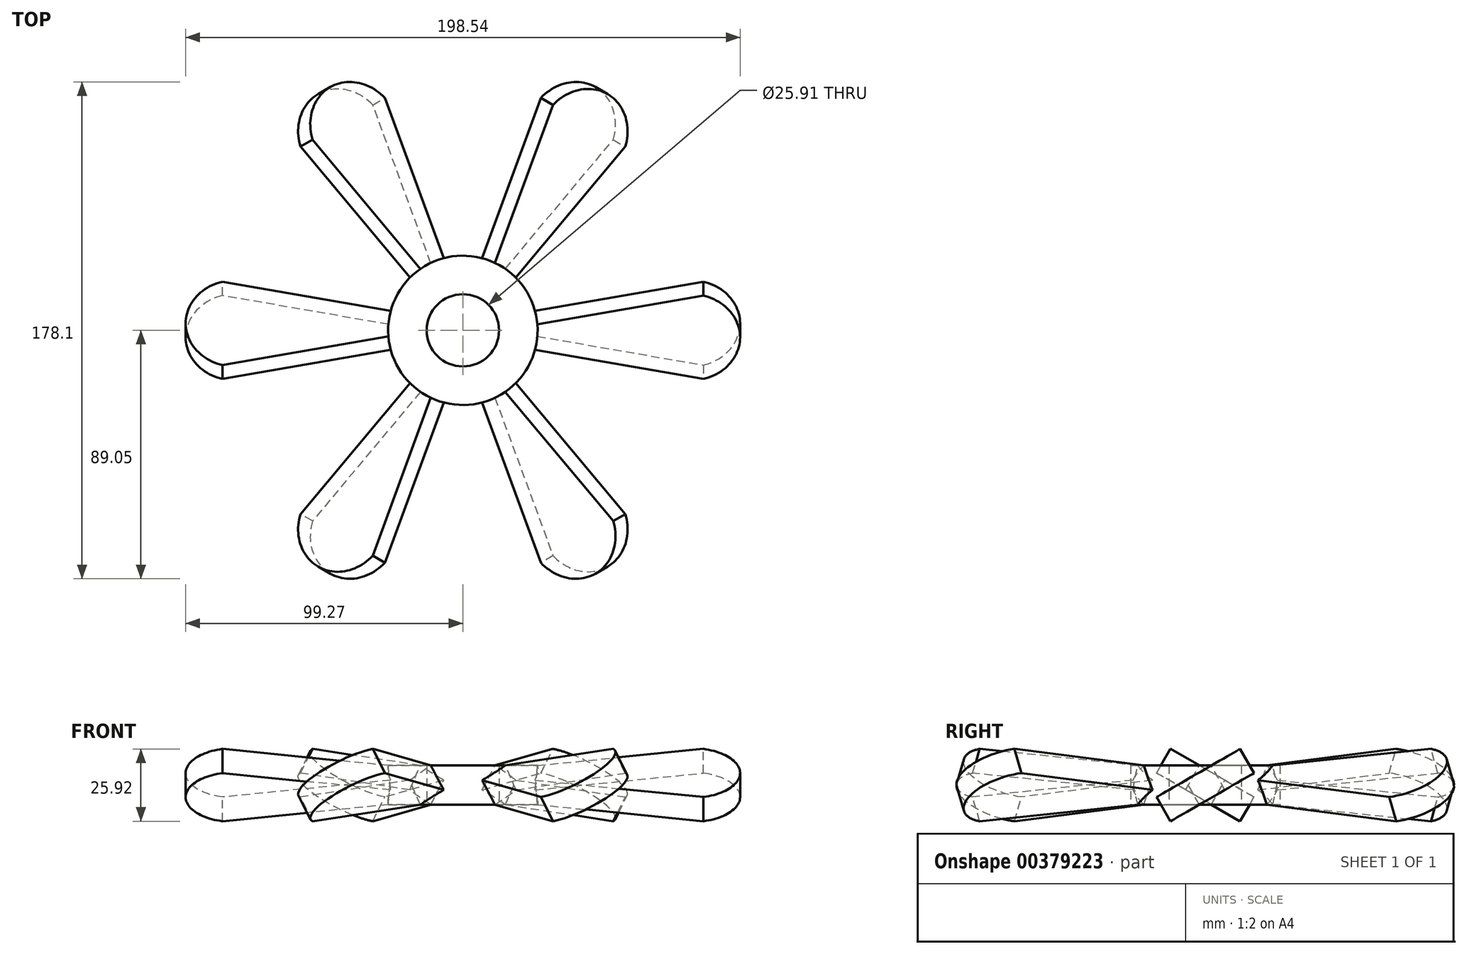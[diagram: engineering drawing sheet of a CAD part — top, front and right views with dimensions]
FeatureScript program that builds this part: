
annotation { "Feature Type Name" : "Feature", "Feature Type Description" : "" }
export const myFeature = defineFeature(function(context is Context, id is Id, definition is map)
    precondition{}
    {
        {
            var Q0;
            Q0=qCreatedBy(makeId("Top.planeOp"),FACE);
            var sketch = newSketch(context, id + "F0", { "sketchPlane" : qUnion([Q0])});
            skLineSegment(sketch, "E0", {"start": v(0, 0) * mm, "end": v(86.12, 17.27) * mm});
            skLineSegment(sketch, "E1", {"start": v(3.06, 0) * mm, "end": v(66.89, 0) * mm, "construction": true});
            skLineSegment(sketch, "E2.MirrorCS", {"start": v(0, 0) * mm, "end": v(86.12, -17.27) * mm});
            skArc(sketch, "E3", {"start": v(86.12, -17.27) * mm, "mid": v(99.27, 0) * mm, "end": v(86.12, 17.27) * mm});
            skSolve(sketch);
        }
        {
            var Q0;
            Q0=makeQuery(id+"F0.imprint","IMPRINT",FACE,{"disambiguationData":[TD([[makeQuery(id+"F0.imprint","IMPRINT",EDGE,{"derivedFrom":sQuery(id+"F0.wireOp",EDGE,"E0")}),-1.0]])]});
            extrude(context, id + "F1", {"entities" : qUnion([Q0]), "endBound" : BoundingType.SYMMETRIC, "oppositeDirection" : true, "depth" : 10 * mm});
        }
        {
            var Q0;
            Q0=qCreatedBy(makeId("Top.planeOp"),FACE);
            var sketch = newSketch(context, id + "F2", { "sketchPlane" : qUnion([Q0])});
            skLineSegment(sketch, "E4", {"start": v(0, 0) * mm, "end": v(111.92, 0) * mm});
            skSolve(sketch);
        }
        {
            var Q0;
            Q0=makeQuery(id+"F1.opExtrude","SWEPT_BODY",BODY,{"disambiguationData":[OSD([sQuery(id+"F0.wireOp",EDGE,"E0"),sQuery(id+"F0.wireOp",EDGE,"E2.MirrorCS"),sQuery(id+"F0.wireOp",EDGE,"E3")])]});
            var Q1;
            Q1=sQuery(id+"F2.wireOp",EDGE,"E4");
            transform(context, id + "F3", {"entities" : qUnion([Q0]), "transformType" : TransformType.ROTATION, "transformAxis" : qUnion([Q1]), "angle" : 30 * degree, "makeCopy" : false});
        }
        {
            var Q0;
            Q0=qCreatedBy(makeId("Front.planeOp"),FACE);
            var sketch = newSketch(context, id + "F4", { "sketchPlane" : qUnion([Q0])});
            skLineSegment(sketch, "E5", {"start": v(0, 0) * mm, "end": v(0, 41.33) * mm, "construction": true});
            skSolve(sketch);
        }
        {
            var Q0;
            Q0=makeQuery(id+"F1.opExtrude","SWEPT_BODY",BODY,{"disambiguationData":[OSD([sQuery(id+"F0.wireOp",EDGE,"E0"),sQuery(id+"F0.wireOp",EDGE,"E2.MirrorCS"),sQuery(id+"F0.wireOp",EDGE,"E3")])]});
            var Q1;
            Q1=sQuery(id+"F4.wireOp",EDGE,"E5");
            circularPattern(context, id + "F5", {"entities" : qUnion([Q0]), "axis" : qUnion([Q1]), "angle" : 360 * degree, "instanceCount" : 6, "equalSpace" : true});
        }
        {
            var Q0;
            Q0=qCreatedBy(makeId("Top.planeOp"),FACE);
            var sketch = newSketch(context, id + "F6", { "sketchPlane" : qUnion([Q0])});
            skCircle(sketch, "E6", {"center": v(0, 0) * mm, "radius": 26.76 * mm});
            skSolve(sketch);
        }
        {
            var Q0;
            Q0=makeQuery(id+"F6.imprint","IMPRINT",FACE,{"disambiguationData":[TD([[makeQuery(id+"F6.imprint","IMPRINT",EDGE,{"derivedFrom":sQuery(id+"F6.wireOp",EDGE,"E6")}),1.0]])]});
            extrude(context, id + "F7", {"entities" : qUnion([Q0]), "endBound" : BoundingType.SYMMETRIC, "depth" : 20 * mm});
        }
        {
            var Q0;
            Q0=makeQuery(id+"F1.opExtrude","SWEPT_BODY",BODY,{"disambiguationData":[OSD([sQuery(id+"F0.wireOp",EDGE,"E0"),sQuery(id+"F0.wireOp",EDGE,"E2.MirrorCS"),sQuery(id+"F0.wireOp",EDGE,"E3")])]});
            var Q1;
            Q1=makeQuery(id+"F5.opPattern","COPY",BODY,{"derivedFrom":makeQuery(id+"F1.opExtrude","SWEPT_BODY",BODY,{"disambiguationData":[OSD([sQuery(id+"F0.wireOp",EDGE,"E0"),sQuery(id+"F0.wireOp",EDGE,"E2.MirrorCS"),sQuery(id+"F0.wireOp",EDGE,"E3")])]}),"instanceName":"1"});
            var Q2;
            Q2=makeQuery(id+"F5.opPattern","COPY",BODY,{"derivedFrom":makeQuery(id+"F1.opExtrude","SWEPT_BODY",BODY,{"disambiguationData":[OSD([sQuery(id+"F0.wireOp",EDGE,"E0"),sQuery(id+"F0.wireOp",EDGE,"E2.MirrorCS"),sQuery(id+"F0.wireOp",EDGE,"E3")])]}),"instanceName":"2"});
            var Q3;
            Q3=makeQuery(id+"F5.opPattern","COPY",BODY,{"derivedFrom":makeQuery(id+"F1.opExtrude","SWEPT_BODY",BODY,{"disambiguationData":[OSD([sQuery(id+"F0.wireOp",EDGE,"E0"),sQuery(id+"F0.wireOp",EDGE,"E2.MirrorCS"),sQuery(id+"F0.wireOp",EDGE,"E3")])]}),"instanceName":"3"});
            var Q4;
            Q4=makeQuery(id+"F5.opPattern","COPY",BODY,{"derivedFrom":makeQuery(id+"F1.opExtrude","SWEPT_BODY",BODY,{"disambiguationData":[OSD([sQuery(id+"F0.wireOp",EDGE,"E0"),sQuery(id+"F0.wireOp",EDGE,"E2.MirrorCS"),sQuery(id+"F0.wireOp",EDGE,"E3")])]}),"instanceName":"4"});
            var Q5;
            Q5=makeQuery(id+"F5.opPattern","COPY",BODY,{"derivedFrom":makeQuery(id+"F1.opExtrude","SWEPT_BODY",BODY,{"disambiguationData":[OSD([sQuery(id+"F0.wireOp",EDGE,"E0"),sQuery(id+"F0.wireOp",EDGE,"E2.MirrorCS"),sQuery(id+"F0.wireOp",EDGE,"E3")])]}),"instanceName":"5"});
            var Q6;
            Q6=makeQuery(id+"F7.opExtrude","SWEPT_BODY",BODY,{"disambiguationData":[OSD([sQuery(id+"F6.wireOp",EDGE,"E6")])]});
            booleanBodies(context, id + "F8", {"operationType" : BooleanOperationType.UNION, "tools" : qUnion([Q0, Q1, Q2, Q3, Q4, Q5, Q6])});
        }
        {
            var Q0;
            {var subQ0=sQuery(id+"F0.wireOp",EDGE,"E0");Q0=makeQuery(id+"F8.opBoolean","INTERSECT",VERTEX,{"derivedFrom":[makeQuery(id+"F5.opPattern","COPY",FACE,{"derivedFrom":makeQuery(id+"F1.opExtrude","SWEPT_FACE",FACE,{"disambiguationData":[OSD([subQ0])]}),"instanceName":"3"}),makeQuery(id+"F5.opPattern","COPY",FACE,{"derivedFrom":makeQuery(id+"F1.opExtrude","CAP_FACE",FACE,{"disambiguationData":[OSD([subQ0,sQuery(id+"F0.wireOp",EDGE,"E2.MirrorCS"),sQuery(id+"F0.wireOp",EDGE,"E3")])],"isStart":true}),"instanceName":"3"}),makeQuery(id+"F7.opExtrude","SWEPT_FACE",FACE,{"disambiguationData":[OSD([sQuery(id+"F6.wireOp",EDGE,"E6")])]})]});}
            var Q1;
            {var subQ0=sQuery(id+"F0.wireOp",EDGE,"E0");Q1=makeQuery(id+"F8.opBoolean","INTERSECT",VERTEX,{"derivedFrom":[makeQuery(id+"F5.opPattern","COPY",FACE,{"derivedFrom":makeQuery(id+"F1.opExtrude","SWEPT_FACE",FACE,{"disambiguationData":[OSD([subQ0])]}),"instanceName":"4"}),makeQuery(id+"F5.opPattern","COPY",FACE,{"derivedFrom":makeQuery(id+"F1.opExtrude","CAP_FACE",FACE,{"disambiguationData":[OSD([subQ0,sQuery(id+"F0.wireOp",EDGE,"E2.MirrorCS"),sQuery(id+"F0.wireOp",EDGE,"E3")])],"isStart":true}),"instanceName":"4"}),makeQuery(id+"F7.opExtrude","SWEPT_FACE",FACE,{"disambiguationData":[OSD([sQuery(id+"F6.wireOp",EDGE,"E6")])]})]});}
            var Q2;
            {var subQ0=sQuery(id+"F0.wireOp",EDGE,"E0");Q2=makeQuery(id+"F8.opBoolean","INTERSECT",VERTEX,{"derivedFrom":[makeQuery(id+"F1.opExtrude","SWEPT_FACE",FACE,{"disambiguationData":[OSD([subQ0])]}),makeQuery(id+"F1.opExtrude","CAP_FACE",FACE,{"disambiguationData":[OSD([subQ0,sQuery(id+"F0.wireOp",EDGE,"E2.MirrorCS"),sQuery(id+"F0.wireOp",EDGE,"E3")])],"isStart":true}),makeQuery(id+"F7.opExtrude","SWEPT_FACE",FACE,{"disambiguationData":[OSD([sQuery(id+"F6.wireOp",EDGE,"E6")])]})]});}
            cPlane(context, id + "F9", {"entities" : qUnion([Q0, Q1, Q2]), "cplaneType" : CPlaneType.THREE_POINT, "offset" : 25 * mm, "width" : 150 * mm, "height" : 150 * mm});
        }
        {
            var Q0;
            Q0=makeQuery(id+"F7.opExtrude","CAP_FACE",FACE,{"disambiguationData":[OSD([sQuery(id+"F6.wireOp",EDGE,"E6")])],"isStart":false});
            var Q1;
            Q1=qCreatedBy(id+"F9.planeOp",FACE);
            extrude(context, id + "F10", {"entities" : qUnion([Q0]), "operationType" : NewBodyOperationType.REMOVE, "endBound" : BoundingType.UP_TO_SURFACE, "oppositeDirection" : true, "endBoundEntityFace" : qUnion([Q1]), "depth" : 25 * mm});
        }
        {
            var Q0;
            {var subQ0=sQuery(id+"F0.wireOp",EDGE,"E2.MirrorCS");Q0=makeQuery(id+"F8.opBoolean","INTERSECT",VERTEX,{"derivedFrom":[makeQuery(id+"F5.opPattern","COPY",FACE,{"derivedFrom":makeQuery(id+"F1.opExtrude","CAP_FACE",FACE,{"disambiguationData":[OSD([sQuery(id+"F0.wireOp",EDGE,"E0"),subQ0,sQuery(id+"F0.wireOp",EDGE,"E3")])],"isStart":false}),"instanceName":"2"}),makeQuery(id+"F5.opPattern","COPY",FACE,{"derivedFrom":makeQuery(id+"F1.opExtrude","SWEPT_FACE",FACE,{"disambiguationData":[OSD([subQ0])]}),"instanceName":"2"}),makeQuery(id+"F7.opExtrude","SWEPT_FACE",FACE,{"disambiguationData":[OSD([sQuery(id+"F6.wireOp",EDGE,"E6")])]})]});}
            var Q1;
            {var subQ0=sQuery(id+"F0.wireOp",EDGE,"E2.MirrorCS");Q1=makeQuery(id+"F8.opBoolean","INTERSECT",VERTEX,{"derivedFrom":[makeQuery(id+"F5.opPattern","COPY",FACE,{"derivedFrom":makeQuery(id+"F1.opExtrude","CAP_FACE",FACE,{"disambiguationData":[OSD([sQuery(id+"F0.wireOp",EDGE,"E0"),subQ0,sQuery(id+"F0.wireOp",EDGE,"E3")])],"isStart":false}),"instanceName":"1"}),makeQuery(id+"F5.opPattern","COPY",FACE,{"derivedFrom":makeQuery(id+"F1.opExtrude","SWEPT_FACE",FACE,{"disambiguationData":[OSD([subQ0])]}),"instanceName":"1"}),makeQuery(id+"F7.opExtrude","SWEPT_FACE",FACE,{"disambiguationData":[OSD([sQuery(id+"F6.wireOp",EDGE,"E6")])]})]});}
            var Q2;
            {var subQ0=sQuery(id+"F0.wireOp",EDGE,"E2.MirrorCS");Q2=makeQuery(id+"F8.opBoolean","INTERSECT",VERTEX,{"derivedFrom":[makeQuery(id+"F5.opPattern","COPY",FACE,{"derivedFrom":makeQuery(id+"F1.opExtrude","CAP_FACE",FACE,{"disambiguationData":[OSD([sQuery(id+"F0.wireOp",EDGE,"E0"),subQ0,sQuery(id+"F0.wireOp",EDGE,"E3")])],"isStart":false}),"instanceName":"5"}),makeQuery(id+"F5.opPattern","COPY",FACE,{"derivedFrom":makeQuery(id+"F1.opExtrude","SWEPT_FACE",FACE,{"disambiguationData":[OSD([subQ0])]}),"instanceName":"5"}),makeQuery(id+"F7.opExtrude","SWEPT_FACE",FACE,{"disambiguationData":[OSD([sQuery(id+"F6.wireOp",EDGE,"E6")])]})]});}
            cPlane(context, id + "F11", {"entities" : qUnion([Q0, Q1, Q2]), "cplaneType" : CPlaneType.THREE_POINT, "offset" : 25 * mm, "width" : 150 * mm, "height" : 150 * mm});
        }
        {
            var Q0;
            Q0=makeQuery(id+"F7.opExtrude","CAP_FACE",FACE,{"disambiguationData":[OSD([sQuery(id+"F6.wireOp",EDGE,"E6")])],"isStart":true});
            var Q1;
            Q1=qCreatedBy(id+"F11.planeOp",FACE);
            extrude(context, id + "F12", {"entities" : qUnion([Q0]), "operationType" : NewBodyOperationType.REMOVE, "endBound" : BoundingType.UP_TO_SURFACE, "oppositeDirection" : true, "endBoundEntityFace" : qUnion([Q1]), "depth" : 25 * mm});
        }
        {
            var Q0;
            Q0=makeQuery(id+"F12.boolean.opBoolean","COPY",FACE,{"derivedFrom":makeQuery(id+"F12.opExtrude","CAP_FACE",FACE,{"disambiguationData":[OSD([sQuery(id+"F6.wireOp",EDGE,"E6")])],"isStart":false})});
            var sketch = newSketch(context, id + "F13", { "sketchPlane" : qUnion([Q0])});
            skCircle(sketch, "E7", {"center": v(0, 0) * mm, "radius": 12.95 * mm});
            skSolve(sketch);
        }
        {
            var Q0;
            Q0 = qSketchRegion(id + "F13", true);
            extrude(context, id + "F14", {"entities" : qUnion([Q0]), "operationType" : NewBodyOperationType.REMOVE, "endBound" : BoundingType.UP_TO_NEXT, "oppositeDirection" : true, "depth" : 25 * mm});
        }
    });
